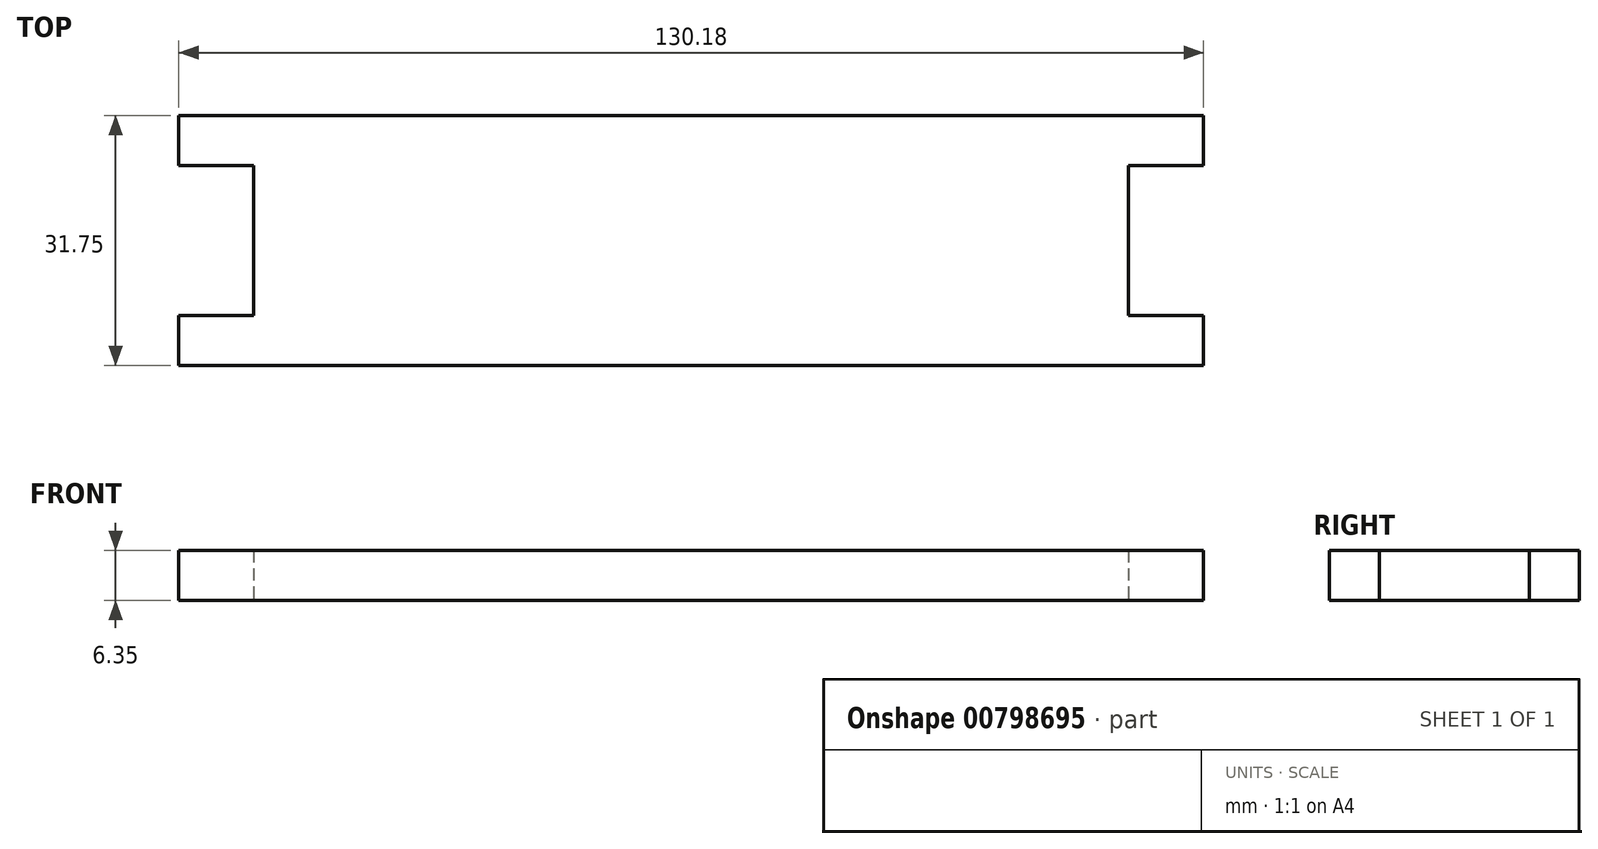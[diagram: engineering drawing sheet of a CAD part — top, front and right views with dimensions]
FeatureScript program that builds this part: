
annotation { "Feature Type Name" : "Feature", "Feature Type Description" : "" }
export const myFeature = defineFeature(function(context is Context, id is Id, definition is map)
    precondition{}
    {
        {
            var Q0;
            Q0=qCreatedBy(makeId("Top.planeOp"),FACE);
            var sketch = newSketch(context, id + "F0", { "sketchPlane" : qUnion([Q0])});
            skLineSegment(sketch, "E0.bottom", {"start": v(0, 0) * mm, "end": v(130.18, 0) * mm});
            skLineSegment(sketch, "E0.top", {"start": v(0, 31.75) * mm, "end": v(130.17, 31.75) * mm});
            skLineSegment(sketch, "E0.left", {"start": v(0, 0) * mm, "end": v(0, 31.75) * mm});
            skLineSegment(sketch, "E0.right", {"start": v(130.18, 0) * mm, "end": v(130.17, 31.75) * mm});
            skLineSegment(sketch, "E1.bottom", {"start": v(0, 6.35) * mm, "end": v(9.52, 6.35) * mm});
            skLineSegment(sketch, "E1.top", {"start": v(0, 25.4) * mm, "end": v(9.52, 25.4) * mm});
            skLineSegment(sketch, "E1.left", {"start": v(0, 6.35) * mm, "end": v(0, 25.4) * mm});
            skLineSegment(sketch, "E1.right", {"start": v(9.53, 6.35) * mm, "end": v(9.53, 25.4) * mm});
            skLineSegment(sketch, "E2.bottom", {"start": v(130.18, 6.35) * mm, "end": v(120.65, 6.35) * mm});
            skLineSegment(sketch, "E2.top", {"start": v(130.17, 25.4) * mm, "end": v(120.65, 25.4) * mm});
            skLineSegment(sketch, "E2.left", {"start": v(130.17, 6.35) * mm, "end": v(130.17, 25.4) * mm});
            skLineSegment(sketch, "E2.right", {"start": v(120.65, 6.35) * mm, "end": v(120.65, 25.4) * mm});
            skSolve(sketch);
        }
        {
            var Q0;
            {var subQ7=sQuery(id+"F0.wireOp",EDGE,"E0.bottom");Q0=makeQuery(id+"F0.imprint","IMPRINT",FACE,{"disambiguationData":[TD([[makeQuery(id+"F0.imprint","IMPRINT",EDGE,{"derivedFrom":subQ7}),1.0]])]});}
            extrude(context, id + "F1", {"entities" : qUnion([Q0]), "depth" : 6.35 * mm, "offsetDistance" : 25.4 * mm});
        }
    });
